FREECAD ASSEMBLY — COMPONENT RECIPES ("RC-Robot-structure-asm")

This assembly document has 35 components, labeled P0..P34 below (a component is one placed body or linked part). 35 of them carry a construction recipe — the FreeCAD feature program that regenerates the part from scratch, quoted from this document or its linked companion documents; the rest are supplied as boundary geometry only. No exploded tour is included for this assembly.
COMPONENT P0 — recipe-attached ("CoinAvant001", a linked part whose construction recipe lives in a companion FreeCAD document of the same project; that document's serialized recipe follows).
Construction recipe (the companion document, serialized — sketch geometry with constraints, then the solid features built on it; lengths are millimeters unless a unit is written):

FCSTD DOCUMENT  (FreeCAD 1.2R20260120 (Git shallow))
Label: RC-Robot-parts-export
License: All rights reserved
LicenseURL: https://en.wikipedia.org/wiki/All_rights_reserved
objects: Part::Feature×18, Part::Mirroring×7, App::Part×1, App::Point×1
note: 25 computed .brp shape members not serialized (recipe doc carries the construction recipe); baked Part::Feature solids carry a one-line shape summary decoded from their .brp

FEATURE [Part::Feature] Part__Feature  label="Moteur"
  Placement = pos=(0,100,4e-16) rot=(1,0,0;3.14159rad)
  shape: bbox 107.1 x 35.7 x 35.7 mm, 15 faces (baked)
FEATURE [Part::Feature] Part__Feature001  label="MotorMount2020"
  Placement = pos=(0,100,0) rot=(0,0,1;0rad)
  shape: bbox 33 x 41.69 x 93.42 mm, 38 faces (baked)
FEATURE [Part::Feature] Part__Feature002  label="CoinLateral"
  shape: bbox 49.87 x 50 x 46.78 mm, 44 faces (baked)
FEATURE [Part::Feature] Part__Feature003  label="CoinAvant"
  shape: bbox 67.87 x 35 x 45.07 mm, 39 faces (baked)
FEATURE [Part::Feature] Part__Feature004  label="SupportAxeRoulement"
  shape: bbox 43.29 x 27 x 91.82 mm, 54 faces (baked)
FEATURE [Part::Feature] Part__Feature005  label="CoinInterieurAvant"
  Placement = pos=(0,109,0) rot=(0,0,1;0rad)
  shape: bbox 47.61 x 27 x 45.08 mm, 55 faces (baked)
FEATURE [Part::Feature] Part__Feature006  label="CoinInterieurArriere"
  shape: bbox 52.12 x 27 x 29.69 mm, 26 faces (baked)
FEATURE [Part::Feature] Part__Feature007  label="EquerrePlateauElec"
  shape: bbox 26.68 x 10 x 21.23 mm, 24 faces (baked)
FEATURE [Part::Feature] Part__Feature008  label="PlateauElec001"
  shape: bbox 169.5 x 90 x 18.92 mm, 62 faces (baked)
FEATURE [Part::Feature] Part__Feature009  label="GardeBoue"
  shape: bbox 26.6 x 90 x 59.82 mm, 54 faces (baked)
FEATURE [Part::Feature] Part__Feature010  label="2020-50mm"
  Placement = pos=(0,-9,0) rot=(0,0,1;0rad)
  shape: bbox 20 x 20 x 50 mm, 51 faces (baked)
FEATURE [Part::Feature] Part__Feature011  label="2020-300mm"
  shape: bbox 20 x 20 x 300 mm, 51 faces (baked)
FEATURE [Part::Feature] Part__Feature012  label="2020-340mm"
  shape: bbox 20 x 20 x 340 mm, 51 faces (baked)
FEATURE [Part::Mirroring] Part__Mirroring  label="CoinAvant (Mirror #1)"
  Base = (273.69,10,18.0708)
  MirrorPlane = -> Part__Feature003 [Face1]
  Normal = (0,1,2e-16)
  Placement = pos=(0,34,0) rot=(0,0,1;0rad)
  Source = -> Part__Feature003
FEATURE [Part::Mirroring] Part__Mirroring001  label="CoinInterieurAvant (Mirror #2)"
  Base = (268.379,82,19.5183)
  MirrorPlane = -> Part__Feature005 [Face8]
  Normal = (0,-1,2e-16)
  Placement = pos=(0,89,0) rot=(0,0,1;0rad)
  Source = -> Part__Feature005
FEATURE [Part::Mirroring] Part__Mirroring002  label="CoinInterieurArriere (Mirror #3)"
  Base = (-70.5769,-27,-24.7156)
  MirrorPlane = -> Part__Feature006 [Face12]
  Normal = (-5e-16,-1,3e-16)
  Source = -> Part__Feature006
FEATURE [Part::Mirroring] Part__Mirroring003  label="CoinLateral (Mirror #4)"
  Base = (-45.1472,-5e-15,49.4406)
  MirrorPlane = -> Part__Feature002 [Face9]
  Normal = (0.0937419,5.2e-15,0.995597)
  Placement = pos=(0,0,-159) rot=(0,0,1;0rad)
  Source = -> Part__Feature002
FEATURE [Part::Mirroring] Part__Mirroring004  label="CoinLateralHG"
  Base = (-71.9119,-20,31.8722)
  MirrorPlane = -> Part__Feature002 [Face11]
  Normal = (0,1,2e-16)
  Source = -> Part__Feature002
FEATURE [Part::Mirroring] Part__Mirroring005  label="CoinLateralBG"
  Base = (-68.1623,-20,-87.3039)
  MirrorPlane = -> Part__Mirroring003 [Face11]
  Normal = (-1e-15,1,-1.06e-14)
  Source = -> Part__Mirroring003
FEATURE [Part::Feature] Part__Feature013  label="CoinLateralHD"
  shape: bbox 49.87 x 50 x 46.78 mm, 44 faces (baked)
FEATURE [Part::Feature] Part__Feature014  label="CoinLateral001"
  shape: bbox 49.87 x 50 x 46.78 mm, 44 faces (baked)
FEATURE [Part::Mirroring] Part__Mirroring006  label="CoinLateralBD"
  Base = (-45.1472,-5e-15,49.4406)
  MirrorPlane = -> Part__Feature014 [Face9]
  Normal = (0.0937419,5.2e-15,0.995597)
  Placement = pos=(0,0,-159) rot=(0,0,1;0rad)
  Source = -> Part__Feature014
FEATURE [Part::Feature] Part__Feature015  label="CoinAvant001"
  shape: bbox 67.87 x 35 x 45.07 mm, 39 faces (baked)
FEATURE [Part::Feature] Part__Feature016  label="CoinInterieurArriere001"
  shape: bbox 52.12 x 27 x 29.69 mm, 26 faces (baked)
FEATURE [Part::Feature] Part__Feature017  label="CoinInterieurAvant001"
  Placement = pos=(0,109,0) rot=(0,0,1;0rad)
  shape: bbox 47.61 x 27 x 45.08 mm, 55 faces (baked)
FEATURE [App::Part] Part  label="motor-mounted"
  Group = -> [Part__Feature001,Part__Feature]
  Origin = -> Origin
FEATURE [App::Point] Origin001  label="Origine"
  Role = Origin
COMPONENT P1 — same part as P0; its construction recipe is shown at P0.
COMPONENT P2 — same part as P0; its construction recipe is shown at P0.
COMPONENT P3 — same part as P0; its construction recipe is shown at P0.
COMPONENT P4 — same part as P0; its construction recipe is shown at P0.
COMPONENT P5 — same part as P0; its construction recipe is shown at P0.
COMPONENT P6 — same part as P0; its construction recipe is shown at P0.
COMPONENT P7 — same part as P0; its construction recipe is shown at P0.
COMPONENT P8 — same part as P0; its construction recipe is shown at P0.
COMPONENT P9 — same part as P0; its construction recipe is shown at P0.
COMPONENT P10 — same part as P0; its construction recipe is shown at P0.
COMPONENT P11 — same part as P0; its construction recipe is shown at P0.
COMPONENT P12 — recipe-attached ("EnsembleRoue", a linked part whose construction recipe lives in a companion FreeCAD document of the same project; that document's serialized recipe follows).
Construction recipe (the companion document, serialized — sketch geometry with constraints, then the solid features built on it; lengths are millimeters unless a unit is written):

FCSTD DOCUMENT  (FreeCAD 1.2R20260204 (Git shallow))
Label: wheel
License: All rights reserved
LicenseURL: https://en.wikipedia.org/wiki/All_rights_reserved
objects: Sketcher::SketchObject×12, PartDesign::Pad×7, App::Point×5, PartDesign::Chamfer×5, PartDesign::Body×4, PartDesign::Pocket×4, PartDesign::Fillet×2, PartDesign::Mirrored×2, App::Link×1, PartDesign::Groove×1, App::Part×1
note: 89 computed .brp shape members not serialized (recipe doc carries the construction recipe); baked Part::Feature solids carry a one-line shape summary decoded from their .brp

FEATURE [App::Link] Link  label="Link(Flasque)"
  LinkPlacement = pos=(-30,6.79493e-06,0) rot=(0,0,1;0rad)
  LinkedObject = -> Body008
  Placement = pos=(-30,6.79493e-06,0) rot=(0,0,1;0rad)
FEATURE [App::Point] Origin045  label="Origine"
  Role = Origin
FEATURE [App::Point] Origin046  label="Origine001"
  Role = Origin
FEATURE [App::Point] Origin047  label="Origine002"
  Role = Origin
FEATURE [App::Point] Origin048  label="Origine003"
  Role = Origin
FEATURE [App::Point] Origin049  label="Origine004"
  Role = Origin
FEATURE [Sketcher::SketchObject] Sketch011
  ArcFitTolerance = 1e-06
  AttachmentSupport = -> [YZ_Plane005]
  ExternalTypes = [0]
  FullyConstrained = true
  MakeInternals = false
  MapMode = 5
  Placement = pos=(0,0,0) rot=(0.57735,0.57735,0.57735;2.0944rad)
  sketch-geometry (2):
    g0: Circle CenterX=0 CenterY=0 CenterZ=0 NormalX=0 NormalY=0 NormalZ=1 AngleXU=0 Radius=54
    g1: Circle CenterX=0 CenterY=0 CenterZ=0 NormalX=0 NormalY=0 NormalZ=1 AngleXU=0 Radius=40
  constraints (4):
    c: Coincident(g0,g-1)
    c: Diameter(g0) = 108
    c: Coincident(g1,g0)
    c: Diameter(g1) = 80
FEATURE [PartDesign::Pad] Pad007
  AlongSketchNormal = false
  Direction = (1,0,0)
  Length = 50
  Length2 = 10
  Placement = pos=(0,0,0) rot=(1,1,1;2.0944rad)
  Profile = -> Sketch011
  ReferenceAxis = -> Sketch011 [N_Axis]
  Refine = true
  SideType = 2
  Suppressed = false
  Type = 0
  Type2 = 0
FEATURE [PartDesign::Fillet] Fillet
  Base = -> Pad007 [Edge3,Edge2]
  BaseFeature = -> Pad007
  Placement = pos=(0,0,0) rot=(1,1,1;2.0944rad)
  Radius = 3
  Refine = true
  SupportTransform = false
  Suppressed = false
  UseAllEdges = false
FEATURE [PartDesign::Chamfer] Chamfer
  Angle = 45
  Base = -> Fillet [Edge10,Face6]
  BaseFeature = -> Fillet
  ChamferType = 0
  FlipDirection = false
  Placement = pos=(0,0,0) rot=(1,1,1;2.0944rad)
  Refine = true
  Size = 1
  Size2 = 1
  SupportTransform = false
  Suppressed = false
  UseAllEdges = false
FEATURE [PartDesign::Body] Body005  label="InsertTPU-Pneu"
  AllowCompound = true
  Group = -> [Sketch011,Pad007,Fillet,Chamfer]
  Origin = -> Origin006
  Tip = -> Chamfer
FEATURE [Sketcher::SketchObject] Sketch012
  ArcFitTolerance = 1e-06
  AttachmentSupport = -> [YZ_Plane006]
  ExternalTypes = [0]
  FullyConstrained = true
  MakeInternals = false
  MapMode = 5
  Placement = pos=(0,0,0) rot=(0.57735,0.57735,0.57735;2.0944rad)
  sketch-geometry (1):
    g0: Circle CenterX=0 CenterY=0 CenterZ=0 NormalX=0 NormalY=0 NormalZ=1 AngleXU=0 Radius=40.5
  constraints (2):
    c: Coincident(g0,g-1)
    c: Diameter(g0) = 81
FEATURE [PartDesign::Pad] Pad008
  AlongSketchNormal = false
  Direction = (1,0,0)
  Length = 50
  Length2 = 10
  Placement = pos=(0,0,0) rot=(1,1,1;2.0944rad)
  Profile = -> Sketch012
  ReferenceAxis = -> Sketch012 [N_Axis]
  Refine = true
  SideType = 2
  Suppressed = false
  Type = 0
  Type2 = 0
FEATURE [Sketcher::SketchObject] Sketch013
  ArcFitTolerance = 1e-06
  AttachmentSupport = -> [YZ_Plane007]
  ExternalTypes = [0]
  FullyConstrained = true
  MakeInternals = false
  MapMode = 5
  Placement = pos=(0,0,0) rot=(0.57735,0.57735,0.57735;2.0944rad)
  sketch-geometry (2):
    g0: Circle CenterX=0 CenterY=0 CenterZ=0 NormalX=0 NormalY=0 NormalZ=1 AngleXU=0 Radius=50
    g1: Circle CenterX=0 CenterY=0 CenterZ=0 NormalX=0 NormalY=0 NormalZ=1 AngleXU=0 Radius=58.75
  constraints (4):
    c: Coincident(g0,g-1)
    c: Diameter(g0) = 100
    c: Coincident(g1,g0)
    c: Diameter(g1) = 117.5
FEATURE [PartDesign::Pad] Pad009
  AlongSketchNormal = false
  Direction = (1,0,0)
  Length = 50
  Length2 = 10
  Placement = pos=(0,0,0) rot=(1,1,1;2.0944rad)
  Profile = -> Sketch013
  ReferenceAxis = -> Sketch013 [N_Axis]
  Refine = true
  SideType = 2
  Suppressed = false
  Type = 0
  Type2 = 0
FEATURE [Sketcher::SketchObject] Sketch014
  ArcFitTolerance = 1e-06
  AttachmentSupport = -> [Pad009]
  ExternalTypes = [0]
  FullyConstrained = true
  MakeInternals = false
  MapMode = 5
  Placement = pos=(25,0,0) rot=(0.57735,0.57735,0.57735;2.0944rad)
  sketch-geometry (1):
    g0: Circle CenterX=0 CenterY=0 CenterZ=0 NormalX=0 NormalY=0 NormalZ=1 AngleXU=0 Radius=36
  constraints (2):
    c: Coincident(g0,g-3)
    c: Diameter(g0) = 72
FEATURE [PartDesign::Pad] Pad010
  AlongSketchNormal = false
  BaseFeature = -> Pad009
  Direction = (1,0,0)
  Length = 2.5
  Length2 = 10
  Placement = pos=(0,0,0) rot=(1,1,1;2.0944rad)
  Profile = -> Sketch014
  ReferenceAxis = -> Sketch014 [N_Axis]
  Refine = true
  SideType = 0
  Suppressed = false
  Type = 0
  Type2 = 0
FEATURE [PartDesign::Mirrored] Mirrored
  BaseFeature = -> Pad010
  MirrorPlane = -> YZ_Plane007
  Originals = -> [Pad010]
  Placement = pos=(0,0,0) rot=(1,1,1;2.0944rad)
  Refine = true
  Suppressed = false
  TransformMode = 0
FEATURE [PartDesign::Fillet] Fillet001
  Base = -> Mirrored [Edge11,Edge10]
  BaseFeature = -> Mirrored
  Placement = pos=(0,0,0) rot=(1,1,1;2.0944rad)
  Radius = 3
  Refine = true
  SupportTransform = false
  Suppressed = false
  UseAllEdges = false
FEATURE [PartDesign::Body] Body007  label="Pneu"
  AllowCompound = true
  Group = -> [Sketch013,Pad009,Sketch014,Pad010,Mirrored,Fillet001]
  Origin = -> Origin009
  Tip = -> Fillet001
FEATURE [Sketcher::SketchObject] Sketch015
  ArcFitTolerance = 1e-06
  AttachmentSupport = -> [Pad008]
  ExternalTypes = [0]
  FullyConstrained = true
  MakeInternals = false
  MapMode = 5
  Placement = pos=(25,0,0) rot=(0.57735,0.57735,0.57735;2.0944rad)
  sketch-geometry (1):
    g0: Circle CenterX=0 CenterY=0 CenterZ=0 NormalX=0 NormalY=0 NormalZ=1 AngleXU=0 Radius=35
  constraints (2):
    c: Coincident(g0,g-1)
    c: Diameter(g0) = 70
FEATURE [PartDesign::Pad] Pad011
  AlongSketchNormal = false
  BaseFeature = -> Pad008
  Direction = (1,0,0)
  Length = 2
  Length2 = 10
  Placement = pos=(0,0,0) rot=(1,1,1;2.0944rad)
  Profile = -> Sketch015
  ReferenceAxis = -> Sketch015 [N_Axis]
  Refine = true
  SideType = 0
  Suppressed = false
  Type = 0
  Type2 = 0
FEATURE [PartDesign::Mirrored] Mirrored001
  BaseFeature = -> Pad011
  MirrorPlane = -> YZ_Plane006
  Originals = -> [Pad011]
  Placement = pos=(0,0,0) rot=(1,1,1;2.0944rad)
  Refine = true
  Suppressed = false
  TransformMode = 0
FEATURE [Sketcher::SketchObject] Sketch016
  ArcFitTolerance = 1e-06
  AttachmentSupport = -> [Mirrored001]
  ExternalTypes = [0]
  FullyConstrained = true
  MakeInternals = false
  MapMode = 5
  Placement = pos=(27,0,0) rot=(0.57735,0.57735,0.57735;2.0944rad)
  sketch-geometry (5):
    g0: Circle CenterX=0 CenterY=30 CenterZ=0 NormalX=0 NormalY=0 NormalZ=1 AngleXU=0 Radius=2.2
    g1: Circle CenterX=-30 CenterY=0 CenterZ=0 NormalX=0 NormalY=0 NormalZ=1 AngleXU=0 Radius=2.2
    g2: Circle CenterX=0 CenterY=-30 CenterZ=0 NormalX=0 NormalY=0 NormalZ=1 AngleXU=0 Radius=2.2
    g3: Circle CenterX=30 CenterY=0 CenterZ=0 NormalX=0 NormalY=0 NormalZ=1 AngleXU=0 Radius=2.2
    g4: Circle [constr] CenterX=0 CenterY=0 CenterZ=0 NormalX=0 NormalY=0 NormalZ=1 AngleXU=0 Radius=30
  constraints (14):
    c: PointOnObject(g0,g-2)
    c: PointOnObject(g1,g-1)
    c: PointOnObject(g2,g-2)
    c: PointOnObject(g3,g-1)
    c: Coincident(g4,g-1)
    c: PointOnObject(g0,g4)
    c: PointOnObject(g1,g4)
    c: PointOnObject(g3,g4)
    c: PointOnObject(g2,g4)
    c: Equal(g3,g0)
    c: Equal(g3,g1)
    c: Equal(g3,g2)
    c: Diameter(g3) = 4.4
    c: Diameter(g4) = 60
FEATURE [PartDesign::Pocket] Pocket003
  AlongSketchNormal = false
  BaseFeature = -> Mirrored001
  Direction = (-1,0,0)
  Length = 15
  Length2 = 10
  Placement = pos=(0,0,0) rot=(1,1,1;2.0944rad)
  Profile = -> Sketch016
  ReferenceAxis = -> Sketch016 [N_Axis]
  Refine = true
  SideType = 0
  Suppressed = false
  Type = 1
  Type2 = 0
FEATURE [Sketcher::SketchObject] Sketch017
  ArcFitTolerance = 1e-06
  AttachmentSupport = -> [YZ_Plane008]
  ExternalTypes = [0]
  FullyConstrained = true
  MakeInternals = false
  MapMode = 5
  Placement = pos=(0,0,0) rot=(0.57735,0.57735,0.57735;2.0944rad)
  sketch-geometry (6):
    g0: Circle CenterX=0 CenterY=0 CenterZ=0 NormalX=0 NormalY=0 NormalZ=1 AngleXU=0 Radius=25
    g1: Circle CenterX=0 CenterY=0 CenterZ=0 NormalX=0 NormalY=0 NormalZ=1 AngleXU=0 Radius=50
    g2: Circle CenterX=0 CenterY=30 CenterZ=0 NormalX=0 NormalY=0 NormalZ=1 AngleXU=0 Radius=1.6
    g3: Circle CenterX=30 CenterY=0 CenterZ=0 NormalX=0 NormalY=0 NormalZ=1 AngleXU=0 Radius=1.6
    g4: Circle CenterX=-30 CenterY=0 CenterZ=0 NormalX=0 NormalY=0 NormalZ=1 AngleXU=0 Radius=1.6
    g5: Circle CenterX=0 CenterY=-30 CenterZ=0 NormalX=0 NormalY=0 NormalZ=1 AngleXU=0 Radius=1.6
  constraints (12):
    c: Coincident(g0,g-1)
    c: Coincident(g1,g0)
    c: Coincident(g2,g-3)
    c: Coincident(g3,g-6)
    c: Coincident(g4,g-4)
    c: Coincident(g5,g-5)
    c: Equal(g5,g4)
    c: Equal(g5,g2)
    c: Equal(g5,g3)
    c: Diameter(g5) = 3.2
    c: Diameter(g0) = 50
    c: Diameter(g1) = 100
FEATURE [PartDesign::Pad] Pad012
  AlongSketchNormal = false
  Direction = (1,0,0)
  Length = 3
  Length2 = 10
  Placement = pos=(0,0,0) rot=(1,1,1;2.0944rad)
  Profile = -> Sketch017
  ReferenceAxis = -> Sketch017 [N_Axis]
  Refine = true
  SideType = 0
  Suppressed = false
  Type = 0
  Type2 = 0
FEATURE [PartDesign::Body] Body008  label="Flasque"
  AllowCompound = true
  Group = -> [Sketch017,Pad012]
  Origin = -> Origin011
  Placement = pos=(27,0,0) rot=(0,0,1;0rad)
  Tip = -> Pad012
FEATURE [Sketcher::SketchObject] Sketch018
  ArcFitTolerance = 1e-06
  AttachmentSupport = -> [Pocket003]
  ExternalTypes = [0]
  FullyConstrained = true
  MakeInternals = false
  MapMode = 5
  Placement = pos=(27,0,0) rot=(0.57735,0.57735,0.57735;2.0944rad)
  sketch-geometry (3):
    g0: ArcOfCircle CenterX=0 CenterY=0 CenterZ=0 NormalX=0 NormalY=0 NormalZ=1 AngleXU=0 Radius=19.7231 StartAngle=2.88792 EndAngle=8.10766
    g1: LineSegment StartX=-19.0919 StartY=4.94975 StartZ=0 EndX=-4.94975 EndY=19.0919 EndZ=0
    g2: LineSegment [constr] StartX=0 StartY=0 StartZ=0 EndX=-12.0208 EndY=12.0208 EndZ=0
  constraints (8):
    c: Coincident(g0,g-1)
    c: Coincident(g1,g0)
    c: Coincident(g1,g0)
    c: Distance(g1) = 20
    c: Coincident(g2,g0)
    c: Symmetric(g0,g0,g2)
    c: Angle(g-2,g2) = 0.785398
    c: Distance(g2) = 17
FEATURE [PartDesign::Pad] Pad013
  AlongSketchNormal = false
  BaseFeature = -> Pocket003
  Direction = (1,0,0)
  Length = 13
  Length2 = 10
  Placement = pos=(0,0,0) rot=(1,1,1;2.0944rad)
  Profile = -> Sketch018
  ReferenceAxis = -> Sketch018 [N_Axis]
  Refine = true
  SideType = 0
  Suppressed = false
  Type = 0
  Type2 = 0
FEATURE [Sketcher::SketchObject] Sketch019
  ArcFitTolerance = 1e-06
  AttachmentOffset = pos=(0,0,0) rot=(0,0,1;1.5708rad)
  AttachmentSupport = -> [Pad013]
  ExternalTypes = [0]
  FullyConstrained = true
  MakeInternals = false
  MapMode = 5
  Placement = pos=(-2.7e-15,-12.0208,12.0208) rot=(1,0,0;0.785398rad)
  sketch-geometry (2):
    g0: Circle CenterX=35 CenterY=0 CenterZ=0 NormalX=0 NormalY=0 NormalZ=1 AngleXU=0 Radius=2.1
    g1: Circle [constr] CenterX=35 CenterY=0 CenterZ=0 NormalX=0 NormalY=0 NormalZ=1 AngleXU=0 Radius=5
  constraints (5):
    c: PointOnObject(g0,g-1)
    c: Diameter(g0) = 4.2
    c: Coincident(g1,g0)
    c: Tangent(g1,g-3)
    c: Diameter(g1) = 10
FEATURE [Sketcher::SketchObject] Sketch020
  ArcFitTolerance = 1e-06
  AttachmentSupport = -> [Pad013]
  ExternalTypes = [0]
  FullyConstrained = true
  MakeInternals = false
  MapMode = 5
  Placement = pos=(40,0,0) rot=(0.57735,0.57735,0.57735;2.0944rad)
  sketch-geometry (1):
    g0: Circle CenterX=0 CenterY=0 CenterZ=0 NormalX=0 NormalY=0 NormalZ=1 AngleXU=0 Radius=3.2
  constraints (2):
    c: Coincident(g0,g-1)
    c: Diameter(g0) = 6.4
FEATURE [PartDesign::Pocket] Pocket004
  AlongSketchNormal = false
  BaseFeature = -> Pad013
  Direction = (-1,0,0)
  Length = 15
  Length2 = 10
  Placement = pos=(0,0,0) rot=(1,1,1;2.0944rad)
  Profile = -> Sketch020
  ReferenceAxis = -> Sketch020 [N_Axis]
  Refine = true
  SideType = 0
  Suppressed = false
  Type = 1
  Type2 = 0
FEATURE [PartDesign::Pocket] Pocket005
  AlongSketchNormal = false
  BaseFeature = -> Pocket004
  Direction = (0,0.707107,-0.707107)
  Length = 17
  Length2 = 10
  Placement = pos=(0,0,0) rot=(1,1,1;2.0944rad)
  Profile = -> Sketch019
  ReferenceAxis = -> Sketch019 [N_Axis]
  Refine = true
  SideType = 0
  Suppressed = false
  Type = 0
  Type2 = 0
FEATURE [Sketcher::SketchObject] Sketch021
  ArcFitTolerance = 1e-06
  AttachmentSupport = -> [Pocket005]
  ExternalGeometry = -> [Pocket005]
  ExternalTypes = [0]
  FullyConstrained = true
  MakeInternals = false
  MapMode = 5
  Placement = pos=(40,0,0) rot=(0.57735,0.57735,0.57735;2.0944rad)
  sketch-geometry (7):
    g0: LineSegment [constr] StartX=0 StartY=0 StartZ=0 EndX=-12.0208 EndY=12.0208 EndZ=0
    g1: LineSegment StartX=-11.0662 StartY=5.90434 StartZ=0 EndX=-8.66206 EndY=3.50018 EndZ=0
    g2: LineSegment StartX=-8.66206 StartY=3.50018 StartZ=0 EndX=-3.50018 EndY=8.66206 EndZ=0
    g3: LineSegment StartX=-3.50018 StartY=8.66206 StartZ=0 EndX=-5.90434 EndY=11.0662 EndZ=0
    g4: LineSegment StartX=-5.90434 StartY=11.0662 StartZ=0 EndX=-11.0662 EndY=5.90434 EndZ=0
    g5: GeomPoint [constr] X=-7.2832 Y=7.2832 Z=0
    g6: GeomPoint [constr] X=-8.48528 Y=8.48528 Z=0
  constraints (17):
    c: Coincident(g0,g-1)
    c: Symmetric(g-3,g-3,g0)
    c: Coincident(g1,g2)
    c: Coincident(g2,g3)
    c: Coincident(g3,g4)
    c: Coincident(g4,g1)
    c: Parallel(g2,g4)
    c: Parallel(g1,g3)
    c: Symmetric(g2,g1,g5)
    c: PointOnObject(g5,g0)
    c: Perpendicular(g1,g2)
    c: Perpendicular(g0,g4)
    c: Distance(g3) = 3.4
    c: Distance(g2) = 7.3
    c: PointOnObject(g6,g4)
    c: PointOnObject(g6,g0)
    c: Distance(g6,g0) = 5
FEATURE [PartDesign::Pocket] Pocket006
  AlongSketchNormal = false
  BaseFeature = -> Pocket005
  Direction = (-1,0,0)
  Length = 9
  Length2 = 10
  Placement = pos=(0,0,0) rot=(1,1,1;2.0944rad)
  Profile = -> Sketch021
  ReferenceAxis = -> Sketch021 [N_Axis]
  Refine = true
  SideType = 0
  Suppressed = false
  Type = 0
  Type2 = 0
FEATURE [Sketcher::SketchObject] Sketch067
  ArcFitTolerance = 1e-06
  AttachmentSupport = -> [XZ_Plane006]
  ExternalTypes = [0]
  FullyConstrained = true
  MakeInternals = false
  MapMode = 5
  Placement = pos=(0,0,0) rot=(1,0,0;1.5708rad)
  sketch-geometry (8):
    g0: LineSegment StartX=-27.5 StartY=0 StartZ=0 EndX=-27.5 EndY=13.7 EndZ=0
    g1: LineSegment StartX=-27.5 StartY=13.7 StartZ=0 EndX=-26 EndY=13.7 EndZ=0
    g2: LineSegment StartX=-26 StartY=13.7 StartZ=0 EndX=-26 EndY=12.2 EndZ=0
    g3: LineSegment StartX=-26 StartY=12.2 StartZ=0 EndX=-19.3 EndY=12.2 EndZ=0
    g4: LineSegment StartX=-19.3 StartY=12.2 StartZ=0 EndX=-19.3 EndY=8.5 EndZ=0
    g5: LineSegment StartX=-19.3 StartY=8.5 StartZ=0 EndX=0 EndY=8.5 EndZ=0
    g6: LineSegment StartX=0 StartY=8.5 StartZ=0 EndX=0 EndY=0 EndZ=0
    g7: LineSegment StartX=0 StartY=0 StartZ=0 EndX=-27.5 EndY=0 EndZ=0
  constraints (23):
    c: PointOnObject(g0,g-1)
    c: Vertical(g0)
    c: Coincident(g0,g1)
    c: Coincident(g1,g2)
    c: Vertical(g2)
    c: Coincident(g2,g3)
    c: Horizontal(g3)
    c: Coincident(g3,g4)
    c: Vertical(g4)
    c: Coincident(g4,g5)
    c: PointOnObject(g5,g-2)
    c: Horizontal(g5)
    c: Coincident(g5,g6)
    c: Coincident(g6,g-1)
    c: Coincident(g6,g7)
    c: Coincident(g7,g0)
    c: PointOnObject(g0,g-3)
    c: Horizontal(g1)
    c: DistanceX(g1,g1) = 1.5
    c: DistanceX(g0,g3) = 8.2
    c: DistanceY(g0,g0) = 13.7
    c: DistanceY(g2) = 12.2
    c: DistanceY(g4) = 8.5
FEATURE [PartDesign::Groove] Groove
  Angle = 360
  Angle2 = 0
  Axis = (1,0,0)
  Base = (0,0,0)
  BaseFeature = -> Pocket006
  Placement = pos=(0,0,0) rot=(1,1,1;2.0944rad)
  Profile = -> Sketch067
  ReferenceAxis = -> Sketch067 [H_Axis]
  Refine = true
  Reversed = true
  Suppressed = false
  Type = 0
FEATURE [PartDesign::Chamfer] Chamfer025
  Angle = 45
  Base = -> Groove [Edge54]
  BaseFeature = -> Groove
  ChamferType = 0
  FlipDirection = false
  Placement = pos=(0,0,0) rot=(1,1,1;2.0944rad)
  Refine = true
  Size = 1
  Size2 = 1
  SupportTransform = false
  Suppressed = false
  UseAllEdges = false
FEATURE [PartDesign::Chamfer] Chamfer026
  Angle = 45
  Base = -> Chamfer025 [Edge5]
  BaseFeature = -> Chamfer025
  ChamferType = 0
  FlipDirection = false
  Placement = pos=(0,0,0) rot=(1,1,1;2.0944rad)
  Refine = true
  Size = 0.4
  Size2 = 1
  SupportTransform = false
  Suppressed = false
  UseAllEdges = false
FEATURE [PartDesign::Chamfer] Chamfer034
  Angle = 45
  Base = -> Chamfer026 [Edge15,Edge17,Edge18,Edge16,Edge28,Edge24,Edge22,Edge26,Edge14]
  BaseFeature = -> Chamfer026
  ChamferType = 0
  FlipDirection = false
  Placement = pos=(0,0,0) rot=(1,1,1;2.0944rad)
  Refine = true
  Size = 1
  Size2 = 1
  SupportTransform = false
  Suppressed = false
  UseAllEdges = false
FEATURE [PartDesign::Chamfer] Chamfer035
  Angle = 45
  Base = -> Chamfer034 [Edge56,Edge54,Edge57,Edge59]
  BaseFeature = -> Chamfer034
  ChamferType = 0
  FlipDirection = false
  Placement = pos=(0,0,0) rot=(1,1,1;2.0944rad)
  Refine = true
  Size = 1
  Size2 = 1
  SupportTransform = false
  Suppressed = false
  UseAllEdges = false
FEATURE [PartDesign::Body] Body006  label="Core-Wheel"
  AllowCompound = true
  Group = -> [Sketch012,Pad008,Sketch015,Pad011,Mirrored001,Sketch016,Pocket003,Sketch018,Pad013,Sketch019,Sketch020,Pocket004,Pocket005,Sketch021,Pocket006,Sketch067,Groove,Chamfer025,Chamfer026,Chamfer034,Chamfer035]
  Origin = -> Origin007
  Tip = -> Chamfer035
FEATURE [App::Part] Part001  label="EnsembleRoue"
  Group = -> [Body005,Body006,Body007,Body008,Link]
  Origin = -> Origin008
  Placement = pos=(-145,0,0) rot=(0,0,1;0rad)
COMPONENT P13 — same part as P12; its construction recipe is shown at P12.
COMPONENT P14 — same part as P0; its construction recipe is shown at P0.
COMPONENT P15 — same part as P0; its construction recipe is shown at P0.
COMPONENT P16 — same part as P0; its construction recipe is shown at P0.
COMPONENT P17 — same part as P0; its construction recipe is shown at P0.
COMPONENT P18 — same part as P0; its construction recipe is shown at P0.
COMPONENT P19 — same part as P0; its construction recipe is shown at P0.
COMPONENT P20 — same part as P0; its construction recipe is shown at P0.
COMPONENT P21 — same part as P0; its construction recipe is shown at P0.
COMPONENT P22 — same part as P0; its construction recipe is shown at P0.
COMPONENT P23 — same part as P0; its construction recipe is shown at P0.
COMPONENT P24 — same part as P0; its construction recipe is shown at P0.
COMPONENT P25 — same part as P0; its construction recipe is shown at P0.
COMPONENT P26 — same part as P0; its construction recipe is shown at P0.
COMPONENT P27 — same part as P0; its construction recipe is shown at P0.
COMPONENT P28 — same part as P0; its construction recipe is shown at P0.
COMPONENT P29 — same part as P0; its construction recipe is shown at P0.
COMPONENT P30 — same part as P0; its construction recipe is shown at P0.
COMPONENT P31 — recipe-attached ("free-wheel-support", a linked part whose construction recipe lives in a companion FreeCAD document of the same project; that document's serialized recipe follows).
Construction recipe (the companion document, serialized — sketch geometry with constraints, then the solid features built on it; lengths are millimeters unless a unit is written):

FCSTD DOCUMENT  (FreeCAD 1.2R20260204 (Git shallow))
Label: free-wheel-support
License: All rights reserved
LicenseURL: https://en.wikipedia.org/wiki/All_rights_reserved
objects: PartDesign::Chamfer×8, Sketcher::SketchObject×7, PartDesign::Pocket×6, App::Point×1, PartDesign::Pad×1, PartDesign::Body×1
note: 60 computed .brp shape members not serialized (recipe doc carries the construction recipe); baked Part::Feature solids carry a one-line shape summary decoded from their .brp

FEATURE [App::Point] Origin001  label="Origine"
  Role = Origin
FEATURE [Sketcher::SketchObject] Sketch
  ArcFitTolerance = 1e-06
  AttachmentSupport = -> [Origin]
  ExternalTypes = [0]
  FullyConstrained = true
  MakeInternals = false
  MapMode = 5
  Placement = pos=(0,0,0) rot=(1,0,0;1.5708rad)
  sketch-geometry (8):
    g0: LineSegment StartX=0 StartY=0 StartZ=0 EndX=0 EndY=20 EndZ=0
    g1: LineSegment StartX=0 StartY=20 StartZ=0 EndX=-37 EndY=20 EndZ=0
    g2: LineSegment [constr] StartX=-37 StartY=20 StartZ=0 EndX=-37 EndY=0 EndZ=0
    g3: LineSegment [constr] StartX=-37 StartY=0 StartZ=0 EndX=0 EndY=0 EndZ=0
    g4: LineSegment StartX=0 StartY=0 StartZ=0 EndX=20 EndY=0 EndZ=0
    g5: LineSegment StartX=20 StartY=0 StartZ=0 EndX=20 EndY=-8 EndZ=0
    g6: LineSegment StartX=20 StartY=-8 StartZ=0 EndX=-37 EndY=-8 EndZ=0
    g7: LineSegment StartX=-37 StartY=-8 StartZ=0 EndX=-37 EndY=20 EndZ=0
  constraints (22):
    c: Coincident(g0,g1)
    c: Coincident(g1,g2)
    c: Coincident(g2,g3)
    c: Coincident(g3,g0)
    c: Vertical(g0)
    c: Vertical(g2)
    c: Horizontal(g1)
    c: Horizontal(g3)
    c: Coincident(g0,g-1)
    c: DistanceY(g0,g0) = 20
    c: Coincident(g4,g0)
    c: PointOnObject(g4,g-1)
    c: Coincident(g5,g4)
    c: Vertical(g5)
    c: Coincident(g6,g5)
    c: Horizontal(g6)
    c: Coincident(g7,g6)
    c: Coincident(g7,g1)
    c: Vertical(g7)
    c: Distance(g5,g5) = 8
    c: Distance(g4,g4) = 20
    c: DistanceX(g1,g1) = 37
FEATURE [PartDesign::Pad] Pad
  Direction = (0,-1,2e-16)
  Length = 72
  Length2 = 10
  Profile = -> Sketch
  ReferenceAxis = -> Sketch [N_Axis]
  Refine = true
  SideType = 2
  Suppressed = false
  Type = 0
  Type2 = 0
FEATURE [Sketcher::SketchObject] Sketch001
  ArcFitTolerance = 1e-06
  AttachmentSupport = -> [Pad]
  ExternalGeometry = -> [Pad]
  ExternalTypes = [0,0]
  FullyConstrained = true
  MakeInternals = false
  MapMode = 5
  Placement = pos=(0,4.4e-15,20) rot=(0,0,1;0rad)
  sketch-geometry (1):
    g0: Circle CenterX=-18.5 CenterY=5e-16 CenterZ=0 NormalX=0 NormalY=0 NormalZ=1 AngleXU=0 Radius=4.2
  constraints (2):
    c: Symmetric(g-4,g-3,g0)
    c: Diameter(g0) = 8.4
FEATURE [PartDesign::Pocket] Pocket
  BaseFeature = -> Pad
  Direction = (0,0,-1)
  Length = 5
  Length2 = 5
  Profile = -> Sketch001
  ReferenceAxis = -> Sketch001 [N_Axis]
  Refine = true
  SideType = 0
  Suppressed = false
  Type = 1
  Type2 = 0
FEATURE [Sketcher::SketchObject] Sketch002
  ArcFitTolerance = 1e-06
  AttachmentSupport = -> [Pocket]
  ExternalGeometry = -> [Pocket]
  ExternalTypes = [0]
  FullyConstrained = true
  MakeInternals = false
  MapMode = 5
  Placement = pos=(0,-1.8e-15,-8) rot=(1,0,0;3.14159rad)
  sketch-geometry (1):
    g0: Circle CenterX=-18.5 CenterY=0 CenterZ=0 NormalX=0 NormalY=0 NormalZ=1 AngleXU=0 Radius=16.5
  constraints (2):
    c: Coincident(g0,g-3)
    c: Diameter(g0) = 33
FEATURE [PartDesign::Pocket] Pocket001
  BaseFeature = -> Pocket
  Direction = (0,0,1)
  Length = 10
  Length2 = 5
  Profile = -> Sketch002
  ReferenceAxis = -> Sketch002 [N_Axis]
  Refine = true
  SideType = 0
  Suppressed = false
  Type = 0
  Type2 = 0
FEATURE [Sketcher::SketchObject] Sketch003
  ArcFitTolerance = 1e-06
  AttachmentSupport = -> [Pocket001]
  ExternalGeometry = -> [Pocket001]
  ExternalTypes = [0]
  FullyConstrained = true
  MakeInternals = false
  MapMode = 5
  Placement = pos=(0,0,2) rot=(1,0,0;3.14159rad)
  sketch-geometry (7):
    g0: LineSegment StartX=-10.9944 StartY=0 StartZ=0 EndX=-14.7472 EndY=6.5 EndZ=0
    g1: LineSegment StartX=-14.7472 StartY=6.5 StartZ=0 EndX=-22.2528 EndY=6.5 EndZ=0
    g2: LineSegment StartX=-22.2528 StartY=6.5 StartZ=0 EndX=-26.0056 EndY=-1.15e-14 EndZ=0
    g3: LineSegment StartX=-26.0056 StartY=-1.15e-14 StartZ=0 EndX=-22.2528 EndY=-6.5 EndZ=0
    g4: LineSegment StartX=-22.2528 StartY=-6.5 StartZ=0 EndX=-14.7472 EndY=-6.5 EndZ=0
    g5: LineSegment StartX=-14.7472 StartY=-6.5 StartZ=0 EndX=-10.9944 EndY=0 EndZ=0
    g6: Circle [constr] CenterX=-18.5 CenterY=-5e-15 CenterZ=0 NormalX=0 NormalY=0 NormalZ=1 AngleXU=0 Radius=7.50555
  constraints (16):
    c: Coincident(g0,g1)
    c: Coincident(g1,g2)
    c: Coincident(g2,g3)
    c: Coincident(g3,g4)
    c: Coincident(g4,g5)
    c: Coincident(g5,g0)
    c: Equal(g0, g1-g5) x5
    c: PointOnObject(g0,g6)
    c: PointOnObject(g1,g6)
    c: PointOnObject(g2,g6)
    c: PointOnObject(g3,g6)
    c: PointOnObject(g4,g6)
    c: PointOnObject(g5,g6)
    c: Coincident(g6,g-3)
    c: PointOnObject(g5,g-1)
    c: Distance(g4,g1) = 13
FEATURE [PartDesign::Pocket] Pocket002
  BaseFeature = -> Pocket001
  Direction = (0,0,1)
  Length = 6.5
  Length2 = 5
  Profile = -> Sketch003
  ReferenceAxis = -> Sketch003 [N_Axis]
  Refine = true
  SideType = 0
  Suppressed = false
  Type = 0
  Type2 = 0
FEATURE [Sketcher::SketchObject] Sketch004
  ArcFitTolerance = 1e-06
  AttachmentSupport = -> [Pocket002]
  ExternalGeometry = -> [Pocket002]
  ExternalTypes = [0]
  FullyConstrained = true
  MakeInternals = false
  MapMode = 5
  Placement = pos=(0,4.4e-15,20) rot=(0,0,1;0rad)
  sketch-geometry (1):
    g0: Circle CenterX=-18.5 CenterY=0 CenterZ=0 NormalX=0 NormalY=0 NormalZ=1 AngleXU=0 Radius=11.25
  constraints (2):
    c: Coincident(g0,g-3)
    c: Diameter(g0) = 22.5
FEATURE [PartDesign::Pocket] Pocket003
  BaseFeature = -> Pocket002
  Direction = (0,0,-1)
  Length = 1.5
  Length2 = 5
  Profile = -> Sketch004
  ReferenceAxis = -> Sketch004 [N_Axis]
  Refine = true
  SideType = 0
  Suppressed = false
  Type = 0
  Type2 = 0
FEATURE [Sketcher::SketchObject] Sketch005
  ArcFitTolerance = 1e-06
  AttachmentSupport = -> [Pocket003]
  ExternalGeometry = -> [Pocket003]
  ExternalTypes = [0,0]
  FullyConstrained = true
  MakeInternals = false
  MapMode = 5
  Placement = pos=(0,0,-1e-16) rot=(0,0,1;0rad)
  sketch-geometry (3):
    g0: LineSegment [constr] StartX=10 StartY=36 StartZ=0 EndX=10 EndY=-36 EndZ=0
    g1: Circle CenterX=10 CenterY=-26 CenterZ=0 NormalX=0 NormalY=0 NormalZ=1 AngleXU=0 Radius=2.7
    g2: Circle CenterX=10 CenterY=26 CenterZ=0 NormalX=0 NormalY=0 NormalZ=1 AngleXU=0 Radius=2.7
  constraints (7):
    c: Symmetric(g-3,g-3,g0)
    c: Symmetric(g-4,g-4,g0)
    c: PointOnObject(g1,g0)
    c: Symmetric(g2,g1,g-1)
    c: Equal(g2,g1)
    c: Diameter(g2) = 5.4
    c: Distance(g2,g-3) = 10
FEATURE [PartDesign::Pocket] Pocket004
  BaseFeature = -> Pocket003
  Direction = (0,0,-1)
  Length = 10
  Length2 = 5
  Profile = -> Sketch005
  ReferenceAxis = -> Sketch005 [N_Axis]
  Refine = true
  SideType = 0
  Suppressed = false
  Type = 0
  Type2 = 0
FEATURE [Sketcher::SketchObject] Sketch006
  ArcFitTolerance = 1e-06
  AttachmentSupport = -> [Pocket004]
  ExternalGeometry = -> [Pocket004]
  ExternalTypes = [0,0]
  FullyConstrained = true
  MakeInternals = false
  MapMode = 5
  Placement = pos=(0,-1.8e-15,-8) rot=(1,0,0;3.14159rad)
  sketch-geometry (2):
    g0: Circle CenterX=10 CenterY=26 CenterZ=0 NormalX=0 NormalY=0 NormalZ=1 AngleXU=0 Radius=4.75
    g1: Circle CenterX=10 CenterY=-26 CenterZ=0 NormalX=0 NormalY=0 NormalZ=1 AngleXU=0 Radius=4.75
  constraints (4):
    c: Coincident(g0,g-3)
    c: Coincident(g1,g-4)
    c: Equal(g1,g0)
    c: Diameter(g0) = 9.5
FEATURE [PartDesign::Pocket] Pocket005
  BaseFeature = -> Pocket004
  Direction = (0,0,1)
  Length = 1
  Length2 = 5
  Profile = -> Sketch006
  ReferenceAxis = -> Sketch006 [N_Axis]
  Refine = true
  SideType = 0
  Suppressed = false
  Type = 0
  Type2 = 0
FEATURE [PartDesign::Chamfer] Chamfer
  Angle = 45
  Base = -> Pocket005 [Edge4,Edge3]
  BaseFeature = -> Pocket005
  ChamferType = 0
  FlipDirection = false
  Refine = true
  Size = 3
  Size2 = 1
  SupportTransform = false
  Suppressed = false
  UseAllEdges = false
FEATURE [PartDesign::Chamfer] Chamfer001
  Angle = 45
  Base = -> Chamfer [Edge27,Edge24]
  BaseFeature = -> Chamfer
  ChamferType = 0
  FlipDirection = false
  Refine = true
  Size = 4
  Size2 = 1
  SupportTransform = false
  Suppressed = false
  UseAllEdges = false
FEATURE [PartDesign::Chamfer] Chamfer002
  Angle = 45
  Base = -> Chamfer001 [Edge29,Edge15]
  BaseFeature = -> Chamfer001
  ChamferType = 0
  FlipDirection = false
  Refine = true
  Size = 6
  Size2 = 1
  SupportTransform = false
  Suppressed = false
  UseAllEdges = false
FEATURE [PartDesign::Chamfer] Chamfer003
  Angle = 45
  Base = -> Chamfer002 [Edge49]
  BaseFeature = -> Chamfer002
  ChamferType = 0
  FlipDirection = false
  Refine = true
  Size = 3
  Size2 = 1
  SupportTransform = false
  Suppressed = false
  UseAllEdges = false
FEATURE [PartDesign::Chamfer] Chamfer004
  Angle = 45
  Base = -> Chamfer003 [Edge3]
  BaseFeature = -> Chamfer003
  ChamferType = 0
  FlipDirection = false
  Refine = true
  Size = 0.8
  Size2 = 1
  SupportTransform = false
  Suppressed = false
  UseAllEdges = false
FEATURE [PartDesign::Chamfer] Chamfer005
  Angle = 45
  Base = -> Chamfer004 [Edge80,Edge75]
  BaseFeature = -> Chamfer004
  ChamferType = 0
  FlipDirection = false
  Refine = true
  Size = 1
  Size2 = 1
  SupportTransform = false
  Suppressed = false
  UseAllEdges = false
FEATURE [PartDesign::Chamfer] Chamfer006
  Angle = 45
  Base = -> Chamfer005 [Edge83,Edge82,Edge80,Edge81]
  BaseFeature = -> Chamfer005
  ChamferType = 0
  FlipDirection = false
  Refine = true
  Size = 0.6
  Size2 = 1
  SupportTransform = false
  Suppressed = false
  UseAllEdges = false
FEATURE [PartDesign::Chamfer] Chamfer007
  Angle = 45
  Base = -> Chamfer006 [Face15,Face13]
  BaseFeature = -> Chamfer006
  ChamferType = 0
  FlipDirection = false
  Refine = true
  Size = 0.4
  Size2 = 1
  SupportTransform = false
  Suppressed = false
  UseAllEdges = false
FEATURE [PartDesign::Body] Body  label="free-wheel-support"
  AllowCompound = true
  Group = -> [Sketch,Pad,Sketch001,Pocket,Sketch002,Pocket001,Sketch003,Pocket002,Sketch004,Pocket003,Sketch005,Pocket004,Sketch006,Pocket005,Chamfer,Chamfer001,Chamfer002,Chamfer003,Chamfer004,Chamfer005,Chamfer006,Chamfer007]
  Origin = -> Origin
  Tip = -> Chamfer007
COMPONENT P32 — same part as P31; its construction recipe is shown at P31.
COMPONENT P33 — same part as P0; its construction recipe is shown at P0.
COMPONENT P34 — same part as P0; its construction recipe is shown at P0.
PROVENANCE & LICENSES
A FreeCAD (.FCStd) document from a public repository crawl; recipes are the document's own serialized feature recipes (and, for linked parts, companion documents' recipes).
License: as declared in the source repository (recorded in the dataset sidecar).
